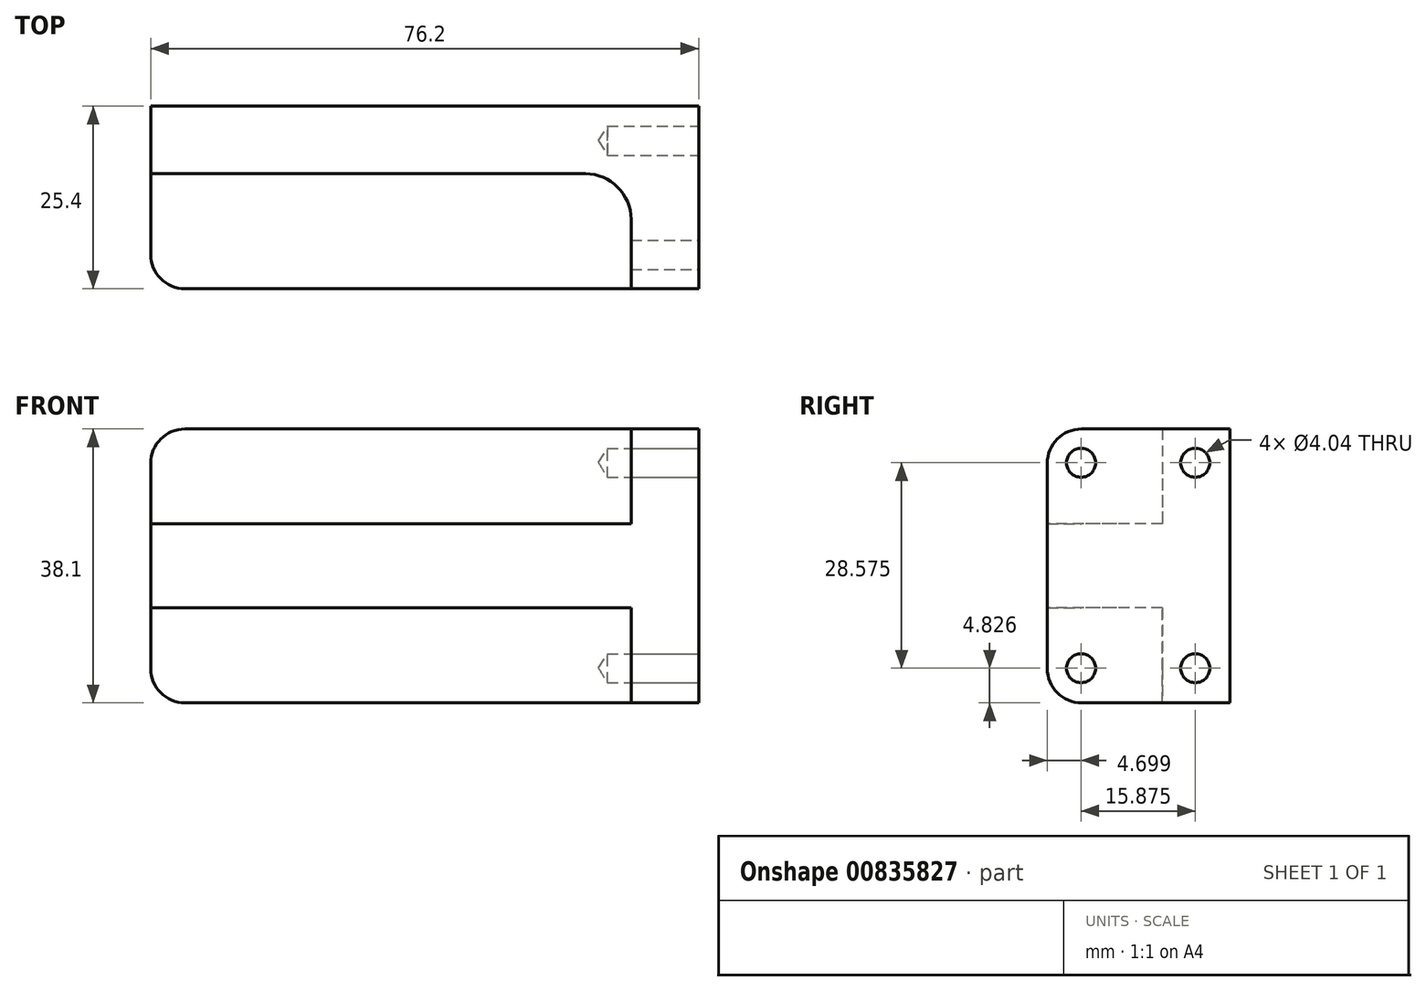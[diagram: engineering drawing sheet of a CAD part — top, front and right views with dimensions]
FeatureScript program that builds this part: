
annotation { "Feature Type Name" : "Feature", "Feature Type Description" : "" }
export const myFeature = defineFeature(function(context is Context, id is Id, definition is map)
    precondition{}
    {
        {
            var Q0;
            Q0=qCreatedBy(makeId("Top.planeOp"),FACE);
            var sketch = newSketch(context, id + "F0", { "sketchPlane" : qUnion([Q0])});
            skLineSegment(sketch, "E0.bottom", {"start": v(38.1, 12.7) * mm, "end": v(-38.1, 12.7) * mm});
            skLineSegment(sketch, "E0.top", {"start": v(38.1, -12.7) * mm, "end": v(-38.1, -12.7) * mm});
            skLineSegment(sketch, "E0.left", {"start": v(38.1, 12.7) * mm, "end": v(38.1, -12.7) * mm});
            skLineSegment(sketch, "E0.right", {"start": v(-38.1, 12.7) * mm, "end": v(-38.1, -12.7) * mm});
            skPoint(sketch, "E0.middle", {"position": v(0, 0) * mm});
            skSolve(sketch);
        }
        {
            var Q0;
            Q0=makeQuery(id+"F0.imprint","IMPRINT",FACE,{"disambiguationData":[TD([[makeQuery(id+"F0.imprint","IMPRINT",EDGE,{"derivedFrom":sQuery(id+"F0.wireOp",EDGE,"E0.bottom")}),1.0]])]});
            extrude(context, id + "F1", {"entities" : qUnion([Q0]), "depth" : 38.1 * mm, "offsetDistance" : 25.4 * mm});
        }
        {
            var Q0;
            Q0=makeQuery(id+"F1.opExtrude","SWEPT_FACE",FACE,{"disambiguationData":[OSD([sQuery(id+"F0.wireOp",EDGE,"E0.top")])]});
            var sketch = newSketch(context, id + "F2", { "sketchPlane" : qUnion([Q0])});
            skLineSegment(sketch, "E1.bottom", {"start": v(-38.1, 38.1) * mm, "end": v(28.7, 38.1) * mm});
            skLineSegment(sketch, "E1.top", {"start": v(-38.1, 24.9) * mm, "end": v(28.7, 24.9) * mm});
            skLineSegment(sketch, "E1.left", {"start": v(-38.1, 38.1) * mm, "end": v(-38.1, 24.9) * mm});
            skLineSegment(sketch, "E1.right", {"start": v(28.7, 38.1) * mm, "end": v(28.7, 24.9) * mm});
            skLineSegment(sketch, "E2", {"start": v(-38.1, 19.05) * mm, "end": v(38.1, 19.05) * mm, "construction": true});
            skLineSegment(sketch, "E3.MirrorCS", {"start": v(-38.1, 0) * mm, "end": v(28.7, 0) * mm});
            skLineSegment(sketch, "E4.MirrorCS", {"start": v(-38.1, 13.2) * mm, "end": v(28.7, 13.2) * mm});
            skLineSegment(sketch, "E5.MirrorCS", {"start": v(28.7, 0) * mm, "end": v(28.7, 13.2) * mm});
            skLineSegment(sketch, "E6.MirrorCS", {"start": v(-38.1, 0) * mm, "end": v(-38.1, 13.2) * mm});
            skSolve(sketch);
        }
        {
            var Q0;
            Q0=makeQuery(id+"F2.imprint","IMPRINT",FACE,{"disambiguationData":[TD([[makeQuery(id+"F2.imprint","IMPRINT",EDGE,{"derivedFrom":sQuery(id+"F2.wireOp",EDGE,"E1.bottom")}),1.0]])]});
            var Q1;
            Q1=makeQuery(id+"F2.imprint","IMPRINT",FACE,{"disambiguationData":[TD([[makeQuery(id+"F2.imprint","IMPRINT",EDGE,{"derivedFrom":sQuery(id+"F2.wireOp",EDGE,"E3.MirrorCS")}),-1.0]])]});
            extrude(context, id + "F3", {"entities" : qUnion([Q0, Q1]), "operationType" : NewBodyOperationType.REMOVE, "oppositeDirection" : true, "depth" : 16 * mm, "offsetDistance" : 25.4 * mm});
        }
        {
            var Q0;
            Q0=makeQuery(id+"F3.boolean.opBoolean","COPY",EDGE,{"derivedFrom":makeQuery(id+"F3.opExtrude","CAP_EDGE",EDGE,{"disambiguationData":[OSD([sQuery(id+"F2.wireOp",EDGE,"E5.MirrorCS")])],"isStart":false})});
            var Q1;
            Q1=makeQuery(id+"F3.boolean.opBoolean","COPY",EDGE,{"derivedFrom":makeQuery(id+"F3.opExtrude","CAP_EDGE",EDGE,{"disambiguationData":[OSD([sQuery(id+"F2.wireOp",EDGE,"E1.right")])],"isStart":false})});
            fillet(context, id + "F4", {"entities" : qUnion([Q0, Q1]), "radius" : 6.35 * mm, "tangentPropagation" : true, "allowEdgeOverflow" : false});
        }
        {
            var Q0;
            Q0=makeQuery(id+"F1.opExtrude","CAP_EDGE",EDGE,{"disambiguationData":[OSD([sQuery(id+"F0.wireOp",EDGE,"E0.top")])],"isStart":false});
            var Q1;
            Q1=makeQuery(id+"F1.opExtrude","CAP_EDGE",EDGE,{"disambiguationData":[OSD([sQuery(id+"F0.wireOp",EDGE,"E0.top")])],"isStart":true});
            fillet(context, id + "F5", {"entities" : qUnion([Q0, Q1]), "radius" : 4.78 * mm, "tangentPropagation" : true, "allowEdgeOverflow" : false});
        }
        {
            var Q0;
            Q0=makeQuery(id+"F1.opExtrude","SWEPT_EDGE",EDGE,{"disambiguationData":[OSD([sQuery(id+"F0.wireOp",EDGE,"E0.top"),sQuery(id+"F0.wireOp",EDGE,"E0.right")])]});
            var Q1;
            Q1=makeQuery(id+"F1.opExtrude","CAP_EDGE",EDGE,{"disambiguationData":[OSD([sQuery(id+"F0.wireOp",EDGE,"E0.right")])],"isStart":false});
            var Q2;
            Q2=makeQuery(id+"F1.opExtrude","CAP_EDGE",EDGE,{"disambiguationData":[OSD([sQuery(id+"F0.wireOp",EDGE,"E0.right")])],"isStart":true});
            fillet(context, id + "F6", {"entities" : qUnion([Q0, Q1, Q2]), "radius" : 4.78 * mm, "tangentPropagation" : true, "allowEdgeOverflow" : false});
        }
        {
            var Q0;
            Q0=makeQuery(id+"F1.opExtrude","SWEPT_FACE",FACE,{"disambiguationData":[OSD([sQuery(id+"F0.wireOp",EDGE,"E0.left")])]});
            var sketch = newSketch(context, id + "F7", { "sketchPlane" : qUnion([Q0])});
            skPoint(sketch, "E7", {"position": v(7.87, 4.83) * mm});
            skPoint(sketch, "E8", {"position": v(-8, 4.83) * mm});
            skPoint(sketch, "E9", {"position": v(-8, 33.4) * mm});
            skPoint(sketch, "E10", {"position": v(7.87, 33.4) * mm});
            skSolve(sketch);
        }
        {
            var Q0;
            Q0=sQuery(id+"F7.wireOp",VERTEX,"E8");
            var Q1;
            Q1=sQuery(id+"F7.wireOp",VERTEX,"E9");
            var Q2;
            Q2=sQuery(id+"F7.wireOp",VERTEX,"E10");
            var Q3;
            Q3=sQuery(id+"F7.wireOp",VERTEX,"E7");
            var Q4;
            Q4=makeQuery(id+"F1.opExtrude","SWEPT_BODY",BODY,{"disambiguationData":[OSD([sQuery(id+"F0.wireOp",EDGE,"E0.bottom"),sQuery(id+"F0.wireOp",EDGE,"E0.top"),sQuery(id+"F0.wireOp",EDGE,"E0.left"),sQuery(id+"F0.wireOp",EDGE,"E0.right")])]});
            hole(context, id + "F8", {"style" : HoleStyle.SIMPLE, "endStyle" : HoleEndStyle.BLIND, "holeDiameter" : 4.04 * mm, "majorDiameter" : 6.35 * mm, "holeDepth" : 12.7 * mm, "isTappedThrough" : true, "tappedDepth" : 12.7 * mm, "tapClearance" : 3, "locations" : qUnion([Q0, Q1, Q2, Q3]), "scope" : qUnion([Q4])});
        }
    });
